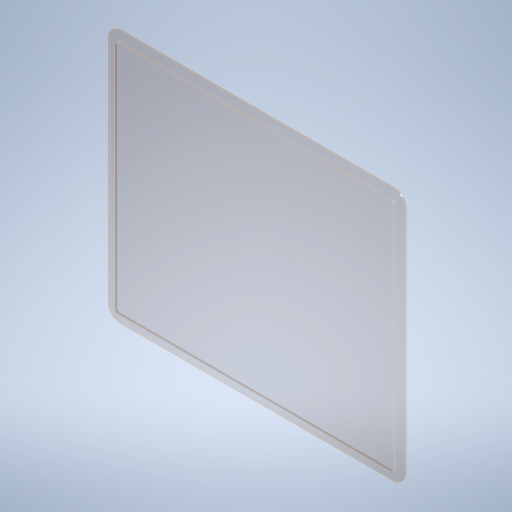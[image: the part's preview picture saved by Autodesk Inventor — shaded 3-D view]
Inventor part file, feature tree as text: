
AUTODESK INVENTOR PART (.ipt)
format: ipt  version: 2024 (Build 280153000, 153)  size: 303,104 bytes
history: native  units: mm
features: extrude x3, sketch x3, projected_geometry x2, fillet x1, plane x1
ambient origin geometry x8: Origin, YZ Plane, XZ Plane, XY Plane, X Axis, Y Axis, Z Axis, Center Point
bodies: Solid1 (feature_tree)
feature tree (10):
  extrude  "Extrusion1"  Depth=4.7625mm
  fillet  "Fillet1"  Radius=4.7625mm
  extrude  "Extrusion2"  Depth=0.5mm
  sketch  "Sketch3"  dims[d6=0.0mm d7=0.0mm d8=12.0mm d9=-3.0mm d10=10.0mm d11=0.0mm]
  plane  "Work Plane1"
  extrude  "Extrusion3"  Depth=12.0mm
  sketch  "Sketch1"  dims[d0=353.0mm d1=298.0mm d2=4.7625mm d3=0.0mm]
  sketch  "Sketch2"  dims[d4=4.0mm d5=0.5mm]
  projected_geometry  "Projected Loop1"
  projected_geometry  "Projected Loop2"
